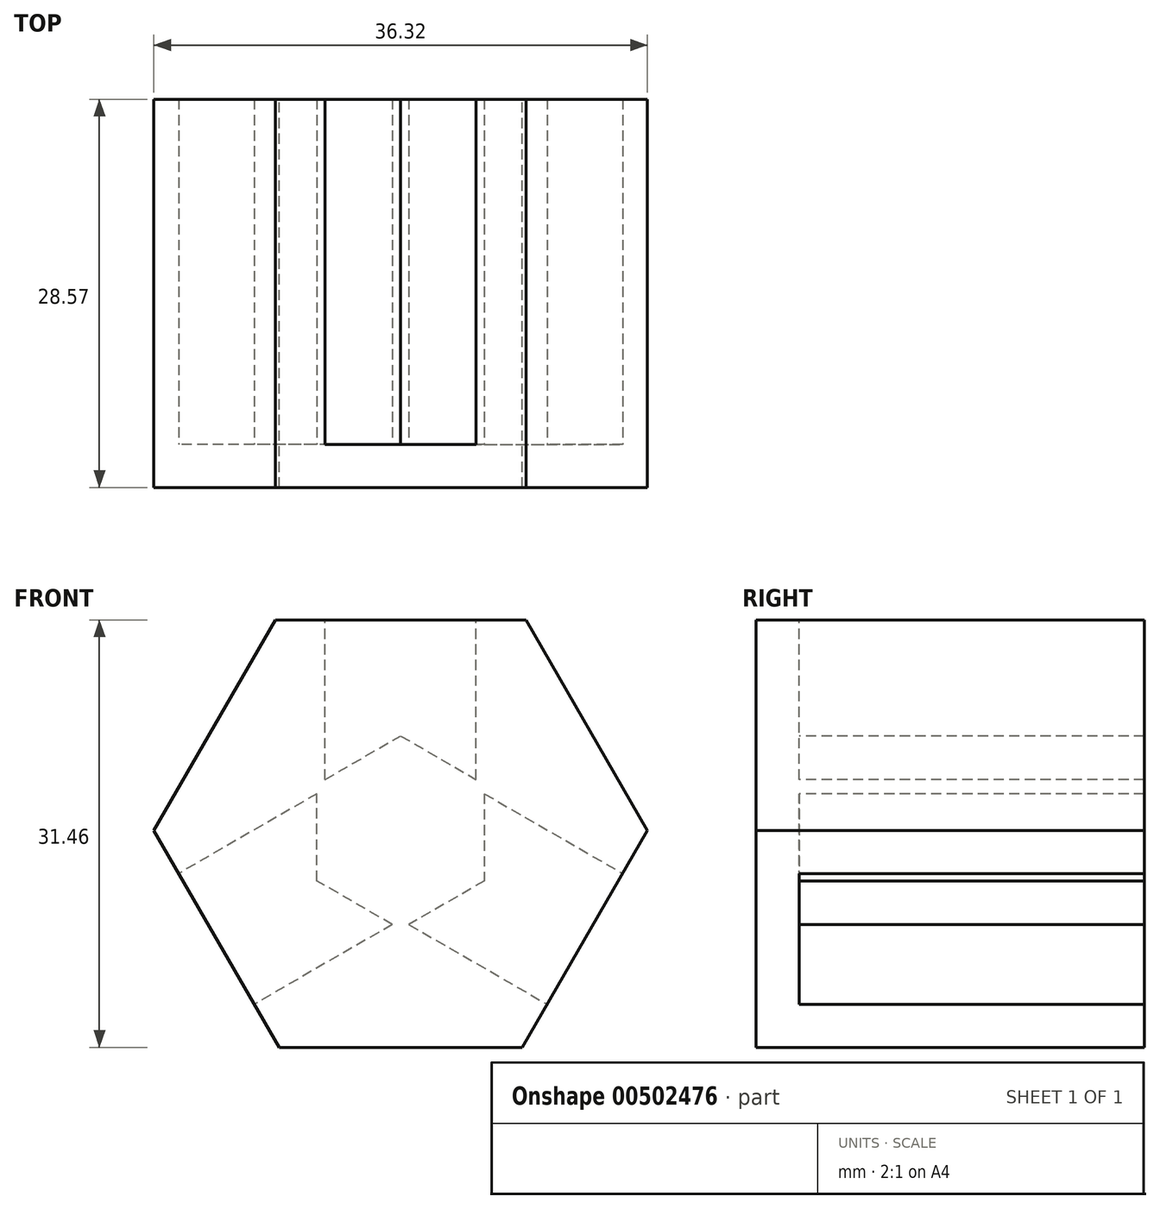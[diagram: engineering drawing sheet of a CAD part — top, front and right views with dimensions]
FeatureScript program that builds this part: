
annotation { "Feature Type Name" : "Feature", "Feature Type Description" : "" }
export const myFeature = defineFeature(function(context is Context, id is Id, definition is map)
    precondition{}
    {
        {
            var Q0;
            Q0=qCreatedBy(makeId("Front.planeOp"),FACE);
            var sketch = newSketch(context, id + "F0", { "sketchPlane" : qUnion([Q0])});
            skSolve(sketch);
        }
        {
            var Q0;
            Q0=qCreatedBy(makeId("Front.planeOp"),FACE);
            var sketch = newSketch(context, id + "F1", { "sketchPlane" : qUnion([Q0])});
            skCircle(sketch, "E0.cCircle", {"center": v(0, 0) * mm, "radius": 44 * mm, "construction": true});
            skLineSegment(sketch, "E0.0", {"start": v(0, -44) * mm, "end": v(-38.1, 22) * mm});
            skLineSegment(sketch, "E0.1", {"start": v(-38.1, 22) * mm, "end": v(38.1, 22) * mm});
            skLineSegment(sketch, "E0.2", {"start": v(38.1, 22) * mm, "end": v(0, -44) * mm});
            skLineSegment(sketch, "E1", {"start": v(-5.56, 3.2) * mm, "end": v(-21.83, -6.19) * mm});
            skLineSegment(sketch, "E2", {"start": v(0, -6.42) * mm, "end": v(-16.27, -15.81) * mm});
            skLineSegment(sketch, "E3", {"start": v(0, -6.42) * mm, "end": v(16.27, -15.81) * mm});
            skLineSegment(sketch, "E4", {"start": v(5.56, 3.2) * mm, "end": v(21.83, -6.19) * mm});
            skLineSegment(sketch, "E5", {"start": v(-5.56, 3.2) * mm, "end": v(-5.56, 22) * mm});
            skLineSegment(sketch, "E6", {"start": v(5.56, 3.2) * mm, "end": v(5.56, 22) * mm});
            skLineSegment(sketch, "E7", {"start": v(5.56, 22) * mm, "end": v(21.83, -6.19) * mm});
            skLineSegment(sketch, "E8", {"start": v(16.27, -15.81) * mm, "end": v(-16.27, -15.81) * mm});
            skLineSegment(sketch, "E9", {"start": v(-21.83, -6.19) * mm, "end": v(-5.56, 22) * mm});
            skLineSegment(sketch, "E10.0", {"start": v(0, -31.3) * mm, "end": v(-27.1, 15.65) * mm});
            skLineSegment(sketch, "E10.1", {"start": v(27.1, 15.65) * mm, "end": v(0, -31.3) * mm});
            skLineSegment(sketch, "E10.2", {"start": v(-27.1, 15.65) * mm, "end": v(27.1, 15.65) * mm});
            skCircle(sketch, "E11.cCircle", {"center": v(0, 0) * mm, "radius": 7.12 * mm, "construction": true});
            skLineSegment(sketch, "E11.0", {"start": v(0, -7.12) * mm, "end": v(-6.16, -3.56) * mm});
            skLineSegment(sketch, "E11.1", {"start": v(-6.16, -3.56) * mm, "end": v(-6.16, 3.56) * mm});
            skLineSegment(sketch, "E11.2", {"start": v(-6.16, 3.56) * mm, "end": v(0, 7.12) * mm});
            skLineSegment(sketch, "E11.3", {"start": v(0, 7.12) * mm, "end": v(6.16, 3.56) * mm});
            skLineSegment(sketch, "E11.4", {"start": v(6.16, 3.56) * mm, "end": v(6.16, -3.56) * mm});
            skLineSegment(sketch, "E11.5", {"start": v(6.16, -3.56) * mm, "end": v(0, -7.12) * mm});
            skSolve(sketch);
        }
        {
            var Q0;
            {var subQ0=sQuery(id+"F1.wireOp",EDGE,"E10.0");var subQ3=sQuery(id+"F1.wireOp",EDGE,"E9");var subQ4=makeQuery(id+"F1.imprint","INTERSECT",VERTEX,{"derivedFrom":[subQ3,subQ0]});Q0=makeQuery(id+"F1.imprint","IMPRINT",FACE,{"disambiguationData":[TD([[makeQuery(id+"F1.imprint","IMPRINT",EDGE,{"disambiguationData":[TD([[subQ4,-1.0]])],"derivedFrom":subQ3}),-1.0]])]});}
            var Q1;
            {var subQ0=sQuery(id+"F1.wireOp",EDGE,"752ecd57-97c3-437e-83ec-500cef74bbd7.1");Q1=makeQuery(id+"F1.imprint","IMPRINT",FACE,{"disambiguationData":[TD([[makeQuery(id+"F1.imprint","IMPRINT",EDGE,{"derivedFrom":subQ0}),1.0]])]});}
            var Q2;
            {var subQ3=sQuery(id+"F1.wireOp",EDGE,"E7");var subQ5=sQuery(id+"F1.wireOp",EDGE,"E10.2");var subQ6=makeQuery(id+"F1.imprint","INTERSECT",VERTEX,{"derivedFrom":[subQ3,subQ5]});Q2=makeQuery(id+"F1.imprint","IMPRINT",FACE,{"disambiguationData":[TD([[makeQuery(id+"F1.imprint","IMPRINT",EDGE,{"disambiguationData":[TD([[subQ6,-1.0]])],"derivedFrom":subQ3}),-1.0]])]});}
            var Q3;
            {var subQ0=sQuery(id+"F1.wireOp",EDGE,"752ecd57-97c3-437e-83ec-500cef74bbd7.2");Q3=makeQuery(id+"F1.imprint","IMPRINT",FACE,{"disambiguationData":[TD([[makeQuery(id+"F1.imprint","IMPRINT",EDGE,{"derivedFrom":subQ0}),1.0]])]});}
            var Q4;
            {var subQ0=sQuery(id+"F1.wireOp",EDGE,"E10.1");var subQ1=sQuery(id+"F1.wireOp",EDGE,"E8");var subQ2=makeQuery(id+"F1.imprint","INTERSECT",VERTEX,{"derivedFrom":[subQ1,subQ0]});Q4=makeQuery(id+"F1.imprint","IMPRINT",FACE,{"disambiguationData":[TD([[makeQuery(id+"F1.imprint","IMPRINT",EDGE,{"disambiguationData":[TD([[subQ2,-1.0]])],"derivedFrom":subQ1}),-1.0]])]});}
            var Q5;
            {var subQ0=sQuery(id+"F1.wireOp",EDGE,"752ecd57-97c3-437e-83ec-500cef74bbd7.0");Q5=makeQuery(id+"F1.imprint","IMPRINT",FACE,{"disambiguationData":[TD([[makeQuery(id+"F1.imprint","IMPRINT",EDGE,{"derivedFrom":subQ0}),1.0]])]});}
            var Q6;
            Q6=makeQuery(id+"F0.imprint","IMPRINT",FACE,{"disambiguationData":[TD([[makeQuery(id+"F0.imprint","IMPRINT",EDGE,{"derivedFrom":sQuery(id+"F0.wireOp",EDGE,"af53b8d9-0d2d-4a86-bab4-ab90d6c67ff4.0")}),-1.0]])]});
            var Q7;
            {var subQ3=sQuery(id+"F1.wireOp",EDGE,"E11.4");var subQ5=sQuery(id+"F1.wireOp",EDGE,"E11.3");var subQ6=makeQuery(id+"F1.imprint","INTERSECT",VERTEX,{"derivedFrom":[subQ5,subQ3]});Q7=makeQuery(id+"F1.imprint","IMPRINT",FACE,{"disambiguationData":[TD([[makeQuery(id+"F1.imprint","IMPRINT",EDGE,{"disambiguationData":[TD([[subQ6,1.0]])],"derivedFrom":subQ5}),-1.0]])]});}
            var Q8;
            {var subQ3=sQuery(id+"F1.wireOp",EDGE,"E11.1");var subQ5=sQuery(id+"F1.wireOp",EDGE,"E11.2");var subQ6=makeQuery(id+"F1.imprint","INTERSECT",VERTEX,{"derivedFrom":[subQ3,subQ5]});Q8=makeQuery(id+"F1.imprint","IMPRINT",FACE,{"disambiguationData":[TD([[makeQuery(id+"F1.imprint","IMPRINT",EDGE,{"disambiguationData":[TD([[subQ6,1.0]])],"derivedFrom":subQ3}),-1.0]])]});}
            var Q9;
            {var subQ3=sQuery(id+"F1.wireOp",EDGE,"E11.0");var subQ5=sQuery(id+"F1.wireOp",EDGE,"E11.5");var subQ6=makeQuery(id+"F1.imprint","INTERSECT",VERTEX,{"derivedFrom":[subQ3,subQ5]});Q9=makeQuery(id+"F1.imprint","IMPRINT",FACE,{"disambiguationData":[TD([[makeQuery(id+"F1.imprint","IMPRINT",EDGE,{"disambiguationData":[TD([[subQ6,-1.0]])],"derivedFrom":subQ3}),-1.0]])]});}
            var Q10;
            {var subQ12=sQuery(id+"F1.wireOp",EDGE,"E5");var subQ13=sQuery(id+"F1.wireOp",EDGE,"E1");var subQ14=makeQuery(id+"F1.imprint","INTERSECT",VERTEX,{"derivedFrom":[subQ13,subQ12]});Q10=makeQuery(id+"F1.imprint","IMPRINT",FACE,{"disambiguationData":[TD([[makeQuery(id+"F1.imprint","IMPRINT",EDGE,{"disambiguationData":[TD([[subQ14,-1.0]])],"derivedFrom":subQ13}),1.0]])]});}
            var Q11;
            {var subQ1=sQuery(id+"F1.wireOp",EDGE,"E11.2");var subQ3=sQuery(id+"F1.wireOp",EDGE,"E5");var subQ4=makeQuery(id+"F1.imprint","INTERSECT",VERTEX,{"derivedFrom":[subQ3,subQ1]});Q11=makeQuery(id+"F1.imprint","IMPRINT",FACE,{"disambiguationData":[TD([[makeQuery(id+"F1.imprint","IMPRINT",EDGE,{"disambiguationData":[TD([[subQ4,-1.0]])],"derivedFrom":subQ3}),-1.0]])]});}
            var Q12;
            {var subQ0=sQuery(id+"F1.wireOp",EDGE,"E11.1");var subQ6=sQuery(id+"F1.wireOp",EDGE,"E1");var subQ9=makeQuery(id+"F1.imprint","INTERSECT",VERTEX,{"derivedFrom":[subQ6,subQ0]});Q12=makeQuery(id+"F1.imprint","IMPRINT",FACE,{"disambiguationData":[TD([[makeQuery(id+"F1.imprint","IMPRINT",EDGE,{"disambiguationData":[TD([[subQ9,-1.0]])],"derivedFrom":subQ6}),1.0]])]});}
            var Q13;
            {var subQ0=sQuery(id+"F1.wireOp",EDGE,"E11.5");var subQ5=sQuery(id+"F1.wireOp",EDGE,"E3");var subQ6=makeQuery(id+"F1.imprint","INTERSECT",VERTEX,{"derivedFrom":[subQ5,subQ0]});Q13=makeQuery(id+"F1.imprint","IMPRINT",FACE,{"disambiguationData":[TD([[makeQuery(id+"F1.imprint","IMPRINT",EDGE,{"disambiguationData":[TD([[subQ6,-1.0]])],"derivedFrom":subQ5}),1.0]])]});}
            extrude(context, id + "F2", {"entities" : qUnion([Q0, Q1, Q2, Q3, Q4, Q5, Q6, Q7, Q8, Q9, Q10, Q11, Q12, Q13]), "depth" : 3.17 * mm});
        }
        {
            var Q0;
            {var subQ0=sQuery(id+"F1.wireOp",EDGE,"E10.0");var subQ3=sQuery(id+"F1.wireOp",EDGE,"E9");var subQ4=makeQuery(id+"F1.imprint","INTERSECT",VERTEX,{"derivedFrom":[subQ3,subQ0]});Q0=makeQuery(id+"F1.imprint","IMPRINT",FACE,{"disambiguationData":[TD([[makeQuery(id+"F1.imprint","IMPRINT",EDGE,{"disambiguationData":[TD([[subQ4,-1.0]])],"derivedFrom":subQ3}),-1.0]])]});}
            var Q1;
            Q1=makeQuery(id+"F1.imprint","IMPRINT",FACE,{"disambiguationData":[TD([[makeQuery(id+"F1.imprint","IMPRINT",EDGE,{"derivedFrom":sQuery(id+"F1.wireOp",EDGE,"752ecd57-97c3-437e-83ec-500cef74bbd7.0")}),-1.0]])]});
            var Q2;
            {var subQ0=sQuery(id+"F1.wireOp",EDGE,"E10.1");var subQ1=sQuery(id+"F1.wireOp",EDGE,"E8");var subQ2=makeQuery(id+"F1.imprint","INTERSECT",VERTEX,{"derivedFrom":[subQ1,subQ0]});Q2=makeQuery(id+"F1.imprint","IMPRINT",FACE,{"disambiguationData":[TD([[makeQuery(id+"F1.imprint","IMPRINT",EDGE,{"disambiguationData":[TD([[subQ2,-1.0]])],"derivedFrom":subQ1}),-1.0]])]});}
            var Q3;
            {var subQ3=sQuery(id+"F1.wireOp",EDGE,"E7");var subQ5=sQuery(id+"F1.wireOp",EDGE,"E10.2");var subQ6=makeQuery(id+"F1.imprint","INTERSECT",VERTEX,{"derivedFrom":[subQ3,subQ5]});Q3=makeQuery(id+"F1.imprint","IMPRINT",FACE,{"disambiguationData":[TD([[makeQuery(id+"F1.imprint","IMPRINT",EDGE,{"disambiguationData":[TD([[subQ6,-1.0]])],"derivedFrom":subQ3}),-1.0]])]});}
            var Q4;
            {var subQ12=sQuery(id+"F1.wireOp",EDGE,"E5");var subQ13=sQuery(id+"F1.wireOp",EDGE,"E1");var subQ14=makeQuery(id+"F1.imprint","INTERSECT",VERTEX,{"derivedFrom":[subQ13,subQ12]});Q4=makeQuery(id+"F1.imprint","IMPRINT",FACE,{"disambiguationData":[TD([[makeQuery(id+"F1.imprint","IMPRINT",EDGE,{"disambiguationData":[TD([[subQ14,-1.0]])],"derivedFrom":subQ13}),1.0]])]});}
            var Q5;
            {var subQ0=sQuery(id+"F1.wireOp",EDGE,"E6");var subQ1=sQuery(id+"F1.wireOp",EDGE,"E4");var subQ2=makeQuery(id+"F1.imprint","INTERSECT",VERTEX,{"derivedFrom":[subQ1,subQ0]});Q5=makeQuery(id+"F1.imprint","IMPRINT",FACE,{"disambiguationData":[TD([[makeQuery(id+"F1.imprint","IMPRINT",EDGE,{"disambiguationData":[TD([[subQ2,-1.0]])],"derivedFrom":subQ1}),1.0]])]});}
            var Q6;
            {var subQ0=sQuery(id+"F1.wireOp",EDGE,"E3");var subQ1=sQuery(id+"F1.wireOp",EDGE,"E2");var subQ2=makeQuery(id+"F1.imprint","INTERSECT",VERTEX,{"derivedFrom":[subQ1,subQ0]});Q6=makeQuery(id+"F1.imprint","IMPRINT",FACE,{"disambiguationData":[TD([[makeQuery(id+"F1.imprint","IMPRINT",EDGE,{"disambiguationData":[TD([[subQ2,-1.0]])],"derivedFrom":subQ1}),1.0]])]});}
            var Q7;
            {var subQ0=sQuery(id+"F1.wireOp",EDGE,"E5");var subQ1=sQuery(id+"F1.wireOp",EDGE,"E1");var subQ2=makeQuery(id+"F1.imprint","INTERSECT",VERTEX,{"derivedFrom":[subQ1,subQ0]});Q7=makeQuery(id+"F1.imprint","IMPRINT",FACE,{"disambiguationData":[TD([[makeQuery(id+"F1.imprint","IMPRINT",EDGE,{"disambiguationData":[TD([[subQ2,-1.0]])],"derivedFrom":subQ1}),-1.0]])]});}
            extrude(context, id + "F3", {"entities" : qUnion([Q0, Q1, Q2, Q3, Q4, Q5, Q6, Q7]), "operationType" : NewBodyOperationType.ADD, "oppositeDirection" : true, "depth" : 25.4 * mm});
        }
    });
